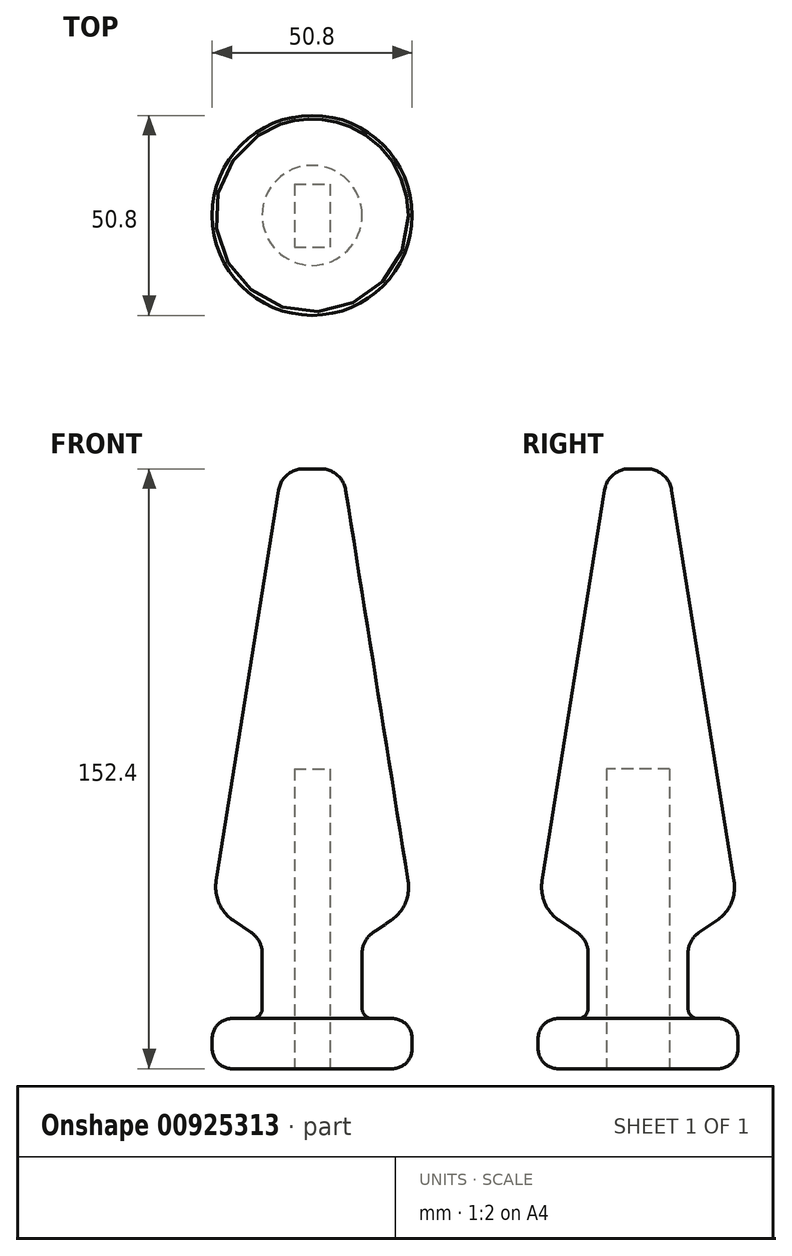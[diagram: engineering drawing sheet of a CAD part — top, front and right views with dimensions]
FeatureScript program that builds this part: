
annotation { "Feature Type Name" : "Feature", "Feature Type Description" : "" }
export const myFeature = defineFeature(function(context is Context, id is Id, definition is map)
    precondition{}
    {
        {
            var Q0;
            Q0=qCreatedBy(makeId("Front.planeOp"),FACE);
            var sketch = newSketch(context, id + "F0", { "sketchPlane" : qUnion([Q0])});
            skLineSegment(sketch, "E0", {"start": v(0, 152.4) * mm, "end": v(0, 0) * mm});
            skLineSegment(sketch, "E1", {"start": v(8.5, 147.05) * mm, "end": v(24.38, 47.68) * mm});
            skLineSegment(sketch, "E2", {"start": v(20.02, 37.64) * mm, "end": v(15.5, 34.6) * mm});
            skLineSegment(sketch, "E3", {"start": v(12.7, 29.34) * mm, "end": v(12.7, 15.28) * mm});
            skLineSegment(sketch, "E4", {"start": v(15.24, 12.74) * mm, "end": v(20.32, 12.74) * mm});
            skLineSegment(sketch, "E5", {"start": v(25.4, 7.66) * mm, "end": v(25.4, 5.08) * mm});
            skLineSegment(sketch, "E6", {"start": v(20.32, 0) * mm, "end": v(0, 0) * mm});
            skLineSegment(sketch, "E7", {"start": v(0, 152.4) * mm, "end": v(2.23, 152.4) * mm});
            skPoint(sketch, "E8.visualSharp", {"position": v(25.4, 41.27) * mm});
            skArc(sketch, "E8.filletArc", {"start": v(20.02, 37.64) * mm, "mid": v(23.66, 42.02) * mm, "end": v(24.38, 47.68) * mm});
            skPoint(sketch, "E9.visualSharp", {"position": v(12.7, 32.72) * mm});
            skArc(sketch, "E9.filletArc", {"start": v(15.5, 34.6) * mm, "mid": v(13.44, 32.32) * mm, "end": v(12.7, 29.34) * mm});
            skPoint(sketch, "E10.visualSharp", {"position": v(25.4, 12.74) * mm});
            skArc(sketch, "E10.filletArc", {"start": v(25.4, 7.66) * mm, "mid": v(23.91, 11.26) * mm, "end": v(20.32, 12.74) * mm});
            skPoint(sketch, "E11.visualSharp", {"position": v(25.4, 0) * mm});
            skArc(sketch, "E11.filletArc", {"start": v(20.32, 0) * mm, "mid": v(23.91, 1.49) * mm, "end": v(25.4, 5.08) * mm});
            skPoint(sketch, "E12.visualSharp", {"position": v(12.7, 12.74) * mm});
            skArc(sketch, "E12.filletArc", {"start": v(12.7, 15.28) * mm, "mid": v(13.44, 13.49) * mm, "end": v(15.24, 12.74) * mm});
            skPoint(sketch, "E13.visualSharp", {"position": v(7.65, 152.4) * mm});
            skArc(sketch, "E13.filletArc", {"start": v(8.5, 147.05) * mm, "mid": v(6.35, 150.88) * mm, "end": v(2.23, 152.4) * mm});
            skSolve(sketch);
        }
        {
            var Q0;
            Q0=makeQuery(id+"F0.imprint","IMPRINT",FACE,{"disambiguationData":[TD([[makeQuery(id+"F0.imprint","IMPRINT",EDGE,{"derivedFrom":sQuery(id+"F0.wireOp",EDGE,"E0")}),1.0]])]});
            var Q1;
            Q1=sQuery(id+"F0.wireOp",EDGE,"E0");
            revolve(context, id + "F1", {"surfaceOperationType" : NewSurfaceOperationType.NEW, "entities" : qUnion([Q0]), "axis" : qUnion([Q1]), "revolveType" : RevolveType.FULL});
        }
        {
            var Q0;
            Q0=makeQuery(id+"F1.opRevolve","SWEPT_FACE",FACE,{"disambiguationData":[OSD([sQuery(id+"F0.wireOp",EDGE,"E6")])]});
            var sketch = newSketch(context, id + "F2", { "sketchPlane" : qUnion([Q0])});
            skLineSegment(sketch, "E14.bottom", {"start": v(-4.5, -8) * mm, "end": v(4.5, -8) * mm});
            skLineSegment(sketch, "E14.top", {"start": v(-4.5, 8) * mm, "end": v(4.5, 8) * mm});
            skLineSegment(sketch, "E14.left", {"start": v(-4.5, -8) * mm, "end": v(-4.5, 8) * mm});
            skLineSegment(sketch, "E14.right", {"start": v(4.5, -8) * mm, "end": v(4.5, 8) * mm});
            skLineSegment(sketch, "E15", {"start": v(-4.5, 0) * mm, "end": v(0, 0) * mm, "construction": true});
            skSolve(sketch);
        }
        {
            var Q0;
            Q0 = qSketchRegion(id + "F2", true);
            extrude(context, id + "F3", {"entities" : qUnion([Q0]), "operationType" : NewBodyOperationType.REMOVE, "oppositeDirection" : true, "depth" : 76.2 * mm, "offsetDistance" : 25.4 * mm});
        }
    });
